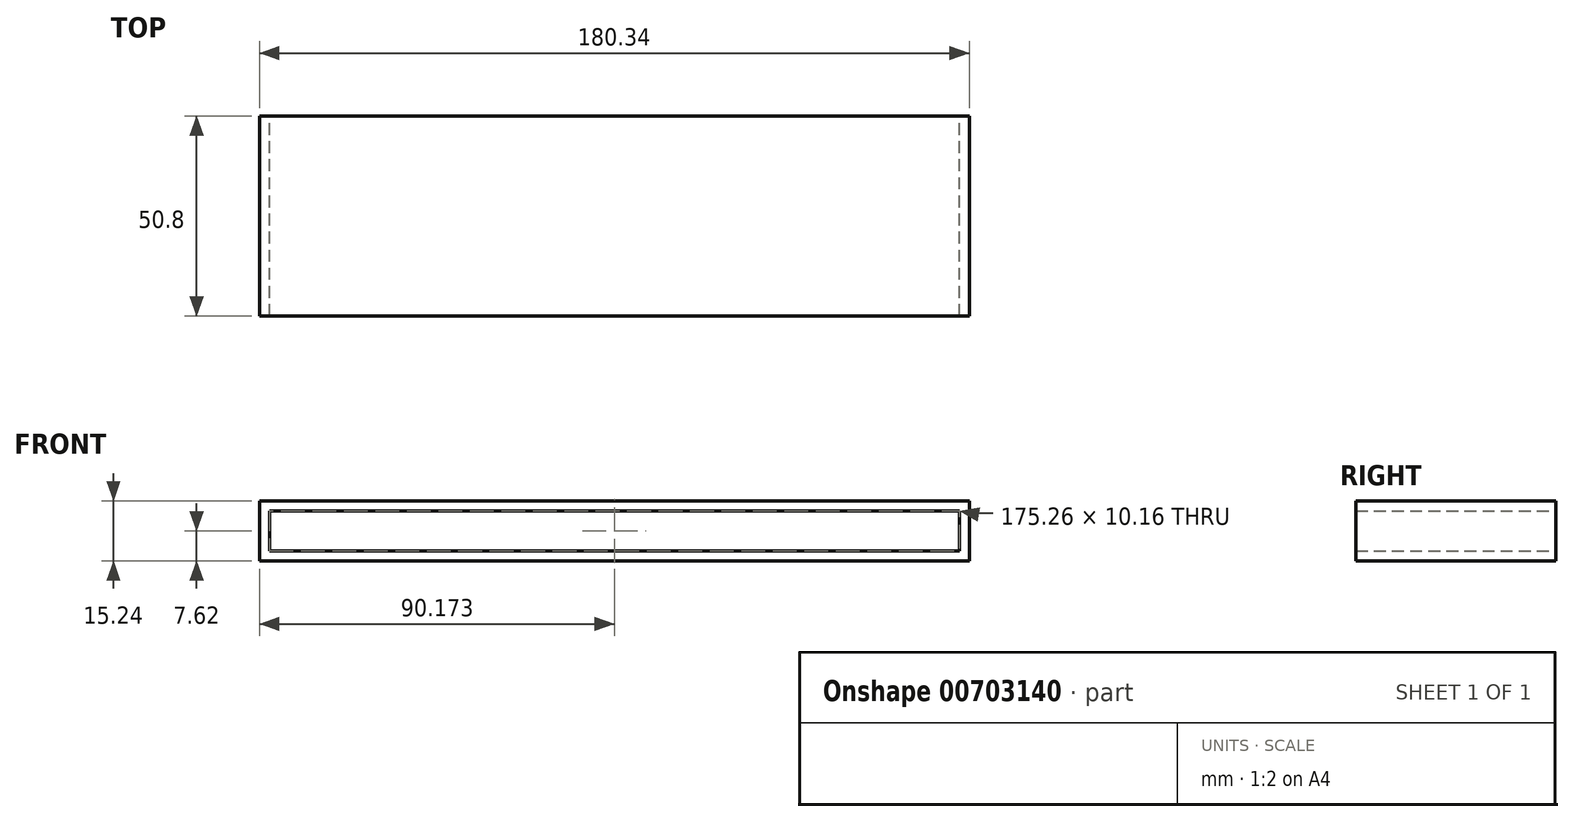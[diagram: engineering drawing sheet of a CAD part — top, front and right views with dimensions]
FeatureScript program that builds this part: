
annotation { "Feature Type Name" : "Feature", "Feature Type Description" : "" }
export const myFeature = defineFeature(function(context is Context, id is Id, definition is map)
    precondition{}
    {
        {
            var Q0;
            Q0=qCreatedBy(makeId("Right.planeOp"),FACE);
            var sketch = newSketch(context, id + "F0", { "sketchPlane" : qUnion([Q0])});
            skLineSegment(sketch, "E0.bottom", {"start": v(-1.27, 1.27) * mm, "end": v(1.27, 1.27) * mm});
            skLineSegment(sketch, "E0.top", {"start": v(-1.27, -1.27) * mm, "end": v(1.27, -1.27) * mm});
            skLineSegment(sketch, "E0.left", {"start": v(-1.27, 1.27) * mm, "end": v(-1.27, -1.27) * mm});
            skLineSegment(sketch, "E0.right", {"start": v(1.27, 1.27) * mm, "end": v(1.27, -1.27) * mm});
            skPoint(sketch, "E0.middle", {"position": v(0, 0) * mm});
            skSolve(sketch);
        }
        {
            var Q0;
            Q0=qCreatedBy(makeId("Front.planeOp"),FACE);
            var sketch = newSketch(context, id + "F1", { "sketchPlane" : qUnion([Q0])});
            skLineSegment(sketch, "E1.bottom", {"start": v(118.1, 12.7) * mm, "end": v(-59.7, 12.7) * mm});
            skLineSegment(sketch, "E1.top", {"start": v(118.1, 0) * mm, "end": v(-59.7, 0) * mm});
            skLineSegment(sketch, "E1.left", {"start": v(118.1, 12.7) * mm, "end": v(118.1, 0) * mm});
            skLineSegment(sketch, "E1.right", {"start": v(-59.7, 12.7) * mm, "end": v(-59.7, 0) * mm});
            skLineSegment(sketch, "E2", {"start": v(29.2, 12.7) * mm, "end": v(29.2, 0) * mm});
            skLineSegment(sketch, "E3", {"start": v(73.64, 12.7) * mm, "end": v(73.64, 0) * mm});
            skLineSegment(sketch, "E4", {"start": v(-15.26, 12.7) * mm, "end": v(-15.26, 0) * mm});
            skSolve(sketch);
        }
        {
            var Q0;
            Q0=makeQuery(id+"F0.imprint","IMPRINT",FACE,{"disambiguationData":[TD([[makeQuery(id+"F0.imprint","IMPRINT",EDGE,{"derivedFrom":sQuery(id+"F0.wireOp",EDGE,"E0.bottom")}),-1.0]])]});
            var Q1;
            Q1=sQuery(id+"F1.wireOp",EDGE,"E1.top");
            var Q2;
            Q2=sQuery(id+"F1.wireOp",EDGE,"E1.left");
            var Q3;
            Q3=sQuery(id+"F1.wireOp",EDGE,"E1.bottom");
            var Q4;
            Q4=sQuery(id+"F1.wireOp",EDGE,"E1.right");
            sweep(context, id + "F2", {"profiles" : qUnion([Q0]), "path" : qUnion([Q1, Q2, Q3, Q4])});
        }
        {
            var Q0;
            Q0=makeQuery(id+"F2.opSweep","SWEPT_FACE",FACE,{"disambiguationData":[OSD([sQuery(id+"F0.wireOp",EDGE,"E0.top"),sQuery(id+"F1.wireOp",EDGE,"E1.bottom")])]});
            var sketch = newSketch(context, id + "F3", { "sketchPlane" : qUnion([Q0])});
            skLineSegment(sketch, "E5.bottom", {"start": v(-16.53, 1.27) * mm, "end": v(-13.99, 1.27) * mm});
            skLineSegment(sketch, "E5.top", {"start": v(-16.53, -1.27) * mm, "end": v(-13.99, -1.27) * mm});
            skLineSegment(sketch, "E5.left", {"start": v(-16.53, 1.27) * mm, "end": v(-16.53, -1.27) * mm});
            skLineSegment(sketch, "E5.right", {"start": v(-13.99, 1.27) * mm, "end": v(-13.99, -1.27) * mm});
            skLineSegment(sketch, "E6.bottom", {"start": v(30.46, 1.27) * mm, "end": v(33, 1.27) * mm});
            skLineSegment(sketch, "E6.top", {"start": v(30.46, -1.27) * mm, "end": v(33, -1.27) * mm});
            skLineSegment(sketch, "E6.left", {"start": v(30.46, 1.27) * mm, "end": v(30.46, -1.27) * mm});
            skLineSegment(sketch, "E6.right", {"start": v(33, 1.27) * mm, "end": v(33, -1.27) * mm});
            skPoint(sketch, "E7.top.end.orphan", {"position": v(29.2, -1.27) * mm});
            skLineSegment(sketch, "E8.bottom", {"start": v(77.45, 1.27) * mm, "end": v(80, 1.27) * mm});
            skLineSegment(sketch, "E8.top", {"start": v(77.45, -1.27) * mm, "end": v(80, -1.27) * mm});
            skLineSegment(sketch, "E8.left", {"start": v(77.45, 1.27) * mm, "end": v(77.45, -1.27) * mm});
            skLineSegment(sketch, "E8.right", {"start": v(80, 1.27) * mm, "end": v(80, -1.27) * mm});
            skSolve(sketch);
        }
        {
            var Q0;
            Q0=makeQuery(id+"F2.opSweep","SWEPT_FACE",FACE,{"disambiguationData":[OSD([sQuery(id+"F0.wireOp",EDGE,"E0.right"),sQuery(id+"F1.wireOp",EDGE,"E1.left")])]});
            var sketch = newSketch(context, id + "F4", { "sketchPlane" : qUnion([Q0])});
            skSolve(sketch);
        }
        {
            var Q0;
            {var subQ0=sQuery(id+"F0.wireOp",EDGE,"E0.right");var subQ1=sQuery(id+"F0.wireOp",EDGE,"E0.bottom");Q0=makeQuery(id+"F4.imprint","IMPRINT",FACE,{"disambiguationData":[TD([[makeQuery(id+"F4.imprint","IMPRINT",EDGE,{"derivedFrom":makeQuery(id+"F2.opSweep","SWEPT_EDGE",EDGE,{"disambiguationData":[OSD([subQ1,subQ0,sQuery(id+"F1.wireOp",EDGE,"E1.bottom")])]})}),-1.0]])]});}
            var sketch = newSketch(context, id + "F5", { "sketchPlane" : qUnion([Q0])});
            skLineSegment(sketch, "E9", {"start": v(-31.85, 14.01) * mm, "end": v(59.19, 0) * mm});
            skLineSegment(sketch, "E10", {"start": v(-31.85, 14.01) * mm, "end": v(-116.25, 0) * mm});
            skSolve(sketch);
        }
        {
            var Q0;
            Q0=makeQuery(id+"F3.imprint","IMPRINT",FACE,{"disambiguationData":[TD([[makeQuery(id+"F3.imprint","IMPRINT",EDGE,{"derivedFrom":sQuery(id+"F3.wireOp",EDGE,"E6.bottom")}),1.0]])]});
            var Q1;
            Q1=sQuery(id+"F5.wireOp",EDGE,"E9");
            var Q2;
            Q2=sQuery(id+"F5.wireOp",EDGE,"E10");
            sweep(context, id + "F6", {"profiles" : qUnion([Q0]), "path" : qUnion([Q1, Q2])});
        }
        {
            var Q0;
            Q0=makeQuery(id+"F6.opSweep","SWEPT_BODY",BODY,{"disambiguationData":[OSD([sQuery(id+"F3.wireOp",EDGE,"E6.bottom"),sQuery(id+"F3.wireOp",EDGE,"E6.top"),sQuery(id+"F3.wireOp",EDGE,"E6.left"),sQuery(id+"F3.wireOp",EDGE,"E6.right"),sQuery(id+"F5.wireOp",EDGE,"E10")])]});
            deleteBodies(context, id + "F7", {"entities" : qUnion([Q0])});
        }
        {
            var Q0;
            Q0=makeQuery(id+"F2.opSweep","SWEPT_FACE",FACE,{"disambiguationData":[OSD([sQuery(id+"F0.wireOp",EDGE,"E0.left"),sQuery(id+"F1.wireOp",EDGE,"E1.left")])]});
            extrude(context, id + "F8", {"entities" : qUnion([Q0]), "operationType" : NewBodyOperationType.ADD, "depth" : 25.4 * mm, "offsetDistance" : 25.4 * mm, "hasSecondDirection" : true, "secondDirectionOppositeDirection" : true, "secondDirectionDepth" : 25.4 * mm});
        }
    });
